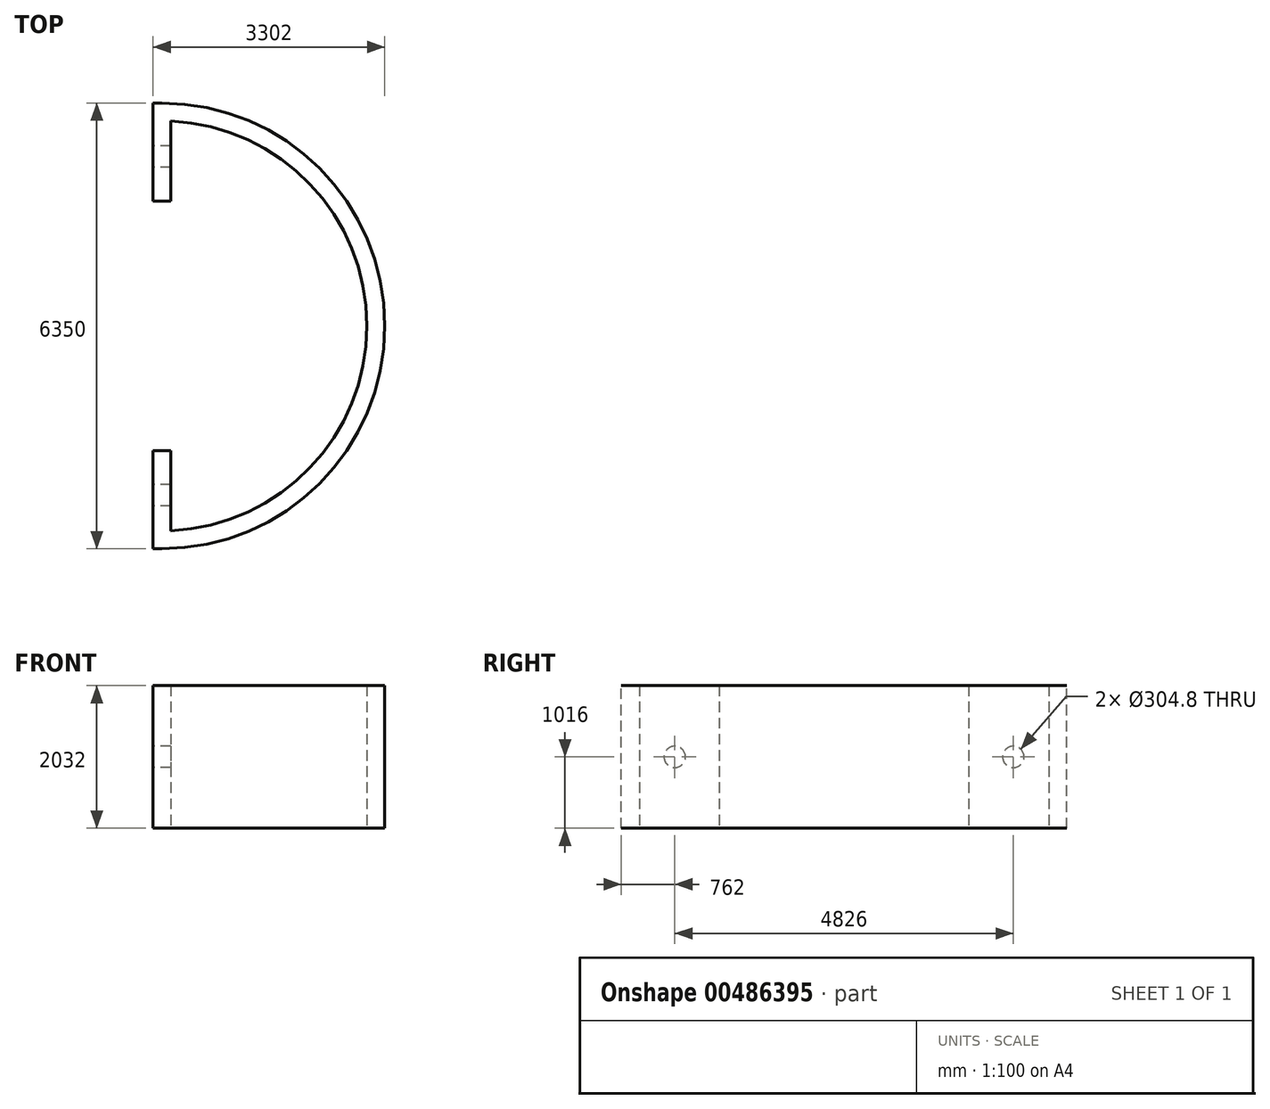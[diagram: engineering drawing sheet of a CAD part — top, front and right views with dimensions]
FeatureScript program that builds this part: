
annotation { "Feature Type Name" : "Feature", "Feature Type Description" : "" }
export const myFeature = defineFeature(function(context is Context, id is Id, definition is map)
    precondition{}
    {
        {
            var Q0;
            Q0=qCreatedBy(makeId("Front.planeOp"),FACE);
            var sketch = newSketch(context, id + "F0", { "sketchPlane" : qUnion([Q0])});
            skLineSegment(sketch, "E0.bottom", {"start": v(-127, 1016) * mm, "end": v(127, 1016) * mm});
            skLineSegment(sketch, "E0.top", {"start": v(-127, -1016) * mm, "end": v(127, -1016) * mm});
            skLineSegment(sketch, "E0.left", {"start": v(-127, 1016) * mm, "end": v(-127, -1016) * mm});
            skLineSegment(sketch, "E0.right", {"start": v(127, 1016) * mm, "end": v(127, -1016) * mm});
            skSolve(sketch);
        }
        {
            var Q0;
            Q0=qCreatedBy(makeId("Top.planeOp"),FACE);
            var sketch = newSketch(context, id + "F1", { "sketchPlane" : qUnion([Q0])});
            skLineSegment(sketch, "E1", {"start": v(0, 0) * mm, "end": v(0, 1270) * mm});
            skArc(sketch, "E2", {"start": v(0, 1270) * mm, "mid": v(3048, -1778) * mm, "end": v(0, -4826) * mm});
            skLineSegment(sketch, "E3", {"start": v(0, -4826) * mm, "end": v(0, -3556) * mm});
            skSolve(sketch);
        }
        {
            var Q0;
            Q0=makeQuery(id+"F0.imprint","IMPRINT",FACE,{"disambiguationData":[TD([[makeQuery(id+"F0.imprint","IMPRINT",EDGE,{"derivedFrom":sQuery(id+"F0.wireOp",EDGE,"E0.bottom")}),-1.0]])]});
            var Q1;
            Q1 = qConstructionFilter(qBodyType(qCreatedBy(id + "F1" ,EDGE), BodyType.WIRE), ConstructionObject.NO);
            sweep(context, id + "F2", {"profiles" : qUnion([Q0]), "path" : qUnion([Q1])});
        }
        {
            var Q0;
            Q0=makeQuery(id+"F2.opSweep","SWEPT_FACE",FACE,{"disambiguationData":[OSD([sQuery(id+"F0.wireOp",EDGE,"E0.left"),sQuery(id+"F1.wireOp",EDGE,"E3")])]});
            var sketch = newSketch(context, id + "F3", { "sketchPlane" : qUnion([Q0])});
            skSolve(sketch);
        }
        {
            var Q0;
            {var subQ1=sQuery(id+"F0.wireOp",EDGE,"E0.left");Q0=makeQuery(id+"F3.imprint","IMPRINT",FACE,{"disambiguationData":[TD([[makeQuery(id+"F3.imprint","IMPRINT",EDGE,{"derivedFrom":makeQuery(id+"F2.opSweep","MID_CAP_EDGE",EDGE,{"disambiguationData":[OSD([subQ1,sQuery(id+"F1.wireOp",VERTEX,"E3.start")])],"capPos":2.0})}),-1.0]])]});}
            var sketch = newSketch(context, id + "F4", { "sketchPlane" : qUnion([Q0])});
            skLineSegment(sketch, "E4", {"start": v(4780.22, 0) * mm, "end": v(-1528.15, 0) * mm, "construction": true});
            skPoint(sketch, "E5", {"position": v(4191, 0) * mm});
            skPoint(sketch, "E6", {"position": v(-635, 0) * mm});
            skSolve(sketch);
        }
        {
            var Q0;
            Q0=sQuery(id+"F4.wireOp",VERTEX,"E5");
            var Q1;
            Q1=sQuery(id+"F4.wireOp",VERTEX,"E6");
            var Q2;
            Q2=makeQuery(id+"F2.opSweep","SWEPT_BODY",BODY,{"disambiguationData":[OSD([sQuery(id+"F0.wireOp",EDGE,"E0.bottom"),sQuery(id+"F0.wireOp",EDGE,"E0.top"),sQuery(id+"F0.wireOp",EDGE,"E0.left"),sQuery(id+"F0.wireOp",EDGE,"E0.right"),sQuery(id+"F1.wireOp",EDGE,"E3")])]});
            hole(context, id + "F5", {"style" : HoleStyle.SIMPLE, "endStyle" : HoleEndStyle.BLIND, "holeDiameter" : 304.8 * mm, "holeDepth" : 254 * mm, "isTappedThrough" : true, "tappedDepth" : 12.7 * mm, "tapClearance" : 3, "locations" : qUnion([Q0, Q1]), "scope" : qUnion([Q2])});
        }
    });
